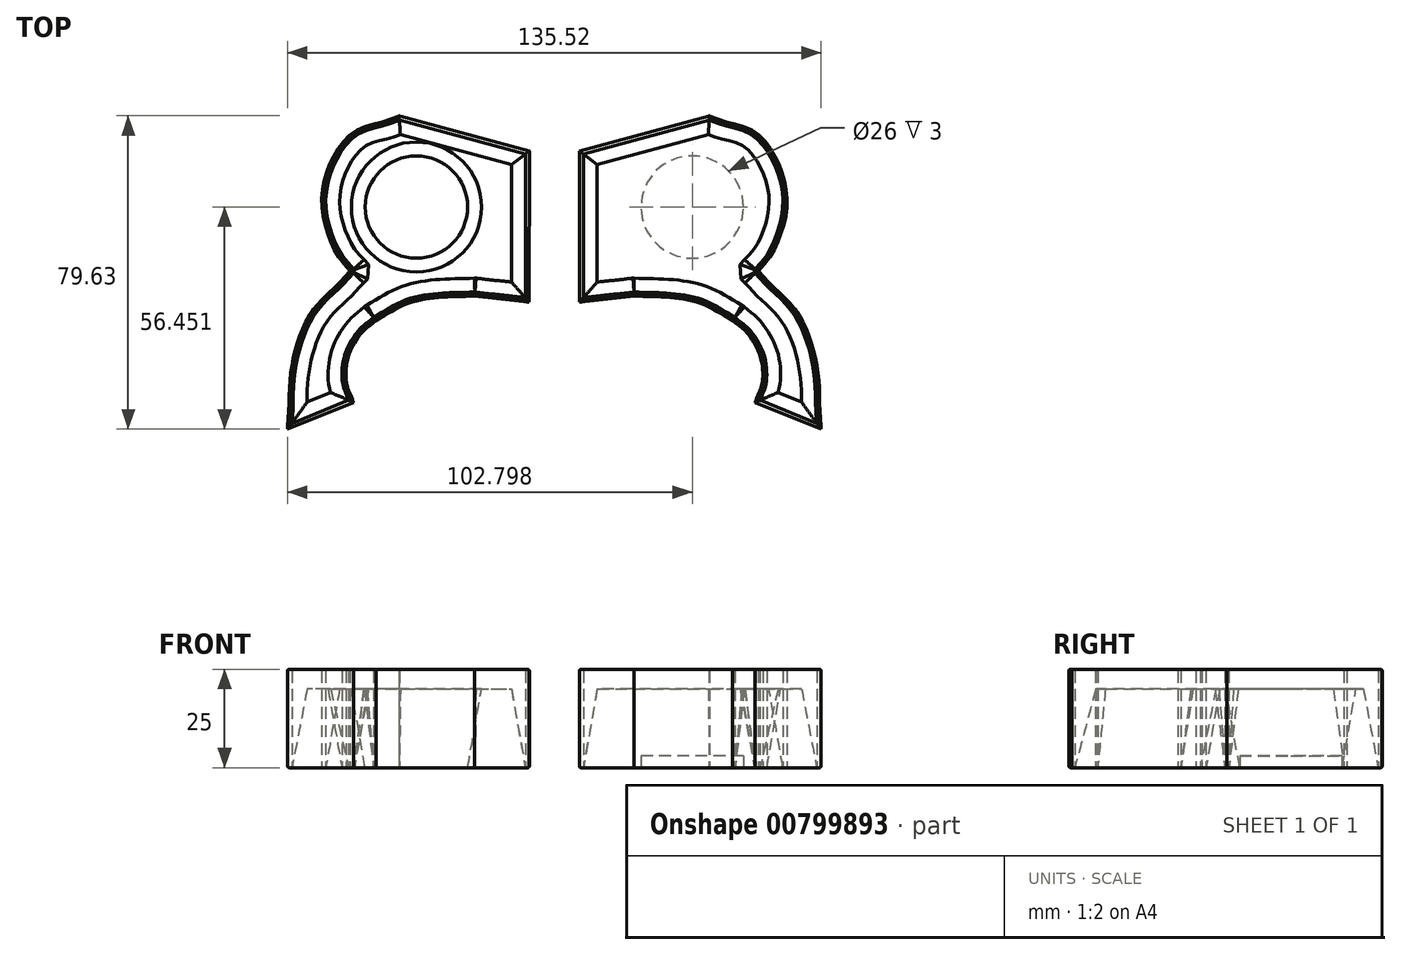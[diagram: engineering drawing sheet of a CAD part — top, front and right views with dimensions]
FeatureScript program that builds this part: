
annotation { "Feature Type Name" : "Feature", "Feature Type Description" : "" }
export const myFeature = defineFeature(function(context is Context, id is Id, definition is map)
    precondition{}
    {
        {
            var Q0;
            Q0=qCreatedBy(makeId("Top.planeOp"),FACE);
            var sketch = newSketch(context, id + "F0", { "sketchPlane" : qUnion([Q0])});
            skFitSpline(sketch, "E0", {"points": [v(6.94, -9.21) * mm, v(8.47, -9.02) * mm, v(11.5, -8.65) * mm, v(15.94, -8.2) * mm, v(18.84, -7.88) * mm, v(20.24, -7.73) * mm]});
            skFitSpline(sketch, "E1", {"points": [v(20.24, -7.73) * mm, v(23.26, -7.85) * mm, v(29.35, -8.1) * mm, v(37.98, -9.9) * mm, v(43, -12.65) * mm, v(45.29, -13.9) * mm]});
            skLineSegment(sketch, "E2", {"start": v(39.35, 38.05) * mm, "end": v(39.24, 38.02) * mm});
            skLineSegment(sketch, "E3", {"start": v(39.24, 38.02) * mm, "end": v(6.36, 29.12) * mm});
            skLineSegment(sketch, "E4", {"start": v(6.36, 29.12) * mm, "end": v(6.38, -9.28) * mm});
            skLineSegment(sketch, "E5", {"start": v(6.38, -9.28) * mm, "end": v(6.94, -9.21) * mm});
            skFitSpline(sketch, "E6", {"points": [v(45.29, -13.9) * mm, v(46.33, -14.78) * mm, v(48.35, -16.47) * mm, v(50.69, -19.57) * mm, v(52.26, -22.94) * mm, v(52.94, -26.6) * mm, v(52.67, -30.5) * mm, v(51.7, -32.98) * mm, v(51.2, -34.29) * mm]});
            skFitSpline(sketch, "E7", {"points": [v(67.73, -40.81) * mm, v(67.44, -36) * mm, v(66.88, -26.6) * mm, v(62.06, -12.45) * mm, v(55.39, -5.2) * mm, v(51.85, -1.37) * mm]});
            skLineSegment(sketch, "E8", {"start": v(51.2, -34.29) * mm, "end": v(50.99, -34.76) * mm});
            skLineSegment(sketch, "E9", {"start": v(50.99, -34.76) * mm, "end": v(67.76, -41.58) * mm});
            skLineSegment(sketch, "E10", {"start": v(67.76, -41.58) * mm, "end": v(67.73, -40.81) * mm});
            skFitSpline(sketch, "E11", {"points": [v(51.85, -1.37) * mm, v(52.8, -0.26) * mm, v(54.73, 1.97) * mm, v(56.78, 5.98) * mm, v(58.84, 12.82) * mm, v(58.12, 22.81) * mm, v(51.17, 33.76) * mm, v(43.4, 36.6) * mm, v(39.46, 38.03) * mm]});
            skLineSegment(sketch, "E12", {"start": v(39.46, 38.03) * mm, "end": v(39.35, 38.05) * mm});
            skLineSegment(sketch, "E13", {"start": v(39.35, 38.05) * mm, "end": v(39.35, 38.05) * mm});
            skLineSegment(sketch, "E14", {"start": v(39.35, 38.05) * mm, "end": v(39.46, 38.03) * mm});
            skFitSpline(sketch, "E15", {"points": [v(39.38, 37.03) * mm, v(43.13, 35.64) * mm, v(50.53, 32.9) * mm, v(57.15, 22.45) * mm, v(57.82, 12.87) * mm, v(55.83, 6.27) * mm, v(53.8, 2.36) * mm, v(51.9, 0.2) * mm, v(50.97, -0.87) * mm]});
            skLineSegment(sketch, "E16", {"start": v(50.97, -0.87) * mm, "end": v(50.81, -1.03) * mm});
            skLineSegment(sketch, "E17", {"start": v(50.81, -1.03) * mm, "end": v(50.86, -1.8) * mm});
            skLineSegment(sketch, "E18", {"start": v(50.86, -1.8) * mm, "end": v(51, -1.93) * mm});
            skLineSegment(sketch, "E19", {"start": v(51, -1.93) * mm, "end": v(50.97, -0.87) * mm});
            skFitSpline(sketch, "E20", {"points": [v(51, -1.93) * mm, v(54.47, -5.64) * mm, v(60.99, -12.63) * mm, v(65.8, -26.3) * mm, v(66.39, -35.4) * mm, v(66.69, -40.07) * mm]});
            skLineSegment(sketch, "E21", {"start": v(66.69, -40.07) * mm, "end": v(52.3, -34.22) * mm});
            skLineSegment(sketch, "E22", {"start": v(52.3, -34.22) * mm, "end": v(66.69, -40.07) * mm});
            skFitSpline(sketch, "E23", {"points": [v(52.3, -34.22) * mm, v(52.78, -32.9) * mm, v(53.7, -30.36) * mm, v(53.91, -26.39) * mm, v(53.2, -22.6) * mm, v(51.55, -19.06) * mm, v(49.1, -15.8) * mm, v(46.98, -14.02) * mm, v(45.9, -13.1) * mm]});
            skLineSegment(sketch, "E24", {"start": v(45.9, -13.1) * mm, "end": v(45.9, -13.1) * mm});
            skLineSegment(sketch, "E25", {"start": v(45.9, -13.1) * mm, "end": v(45.89, -13.1) * mm});
            skLineSegment(sketch, "E26", {"start": v(45.89, -13.1) * mm, "end": v(45.9, -13.1) * mm});
            skFitSpline(sketch, "E27", {"points": [v(45.89, -13.1) * mm, v(43.5, -11.78) * mm, v(38.35, -8.93) * mm, v(29.48, -7.07) * mm, v(23.27, -6.84) * mm, v(20.2, -6.73) * mm]});
            skLineSegment(sketch, "E28", {"start": v(20.2, -6.73) * mm, "end": v(20.18, -6.73) * mm});
            skLineSegment(sketch, "E29", {"start": v(20.18, -6.73) * mm, "end": v(20.15, -6.73) * mm});
            skLineSegment(sketch, "E30", {"start": v(20.15, -6.73) * mm, "end": v(20.2, -6.73) * mm});
            skFitSpline(sketch, "E31", {"points": [v(20.15, -6.73) * mm, v(18.82, -6.88) * mm, v(16.04, -7.2) * mm, v(11.77, -7.63) * mm, v(8.85, -7.98) * mm, v(7.38, -8.16) * mm]});
            skLineSegment(sketch, "E32", {"start": v(7.38, -8.16) * mm, "end": v(7.36, 28.36) * mm});
            skLineSegment(sketch, "E33", {"start": v(7.36, 28.36) * mm, "end": v(39.38, 37.03) * mm});
            skLineSegment(sketch, "E34", {"start": v(39.38, 37.03) * mm, "end": v(39.38, 37.03) * mm});
            skCircle(sketch, "E35", {"center": v(35.04, 14.87) * mm, "radius": 13 * mm});
            skLineSegment(sketch, "E36.MirrorCS", {"start": v(-39.35, 38.05) * mm, "end": v(-39.24, 38.02) * mm});
            skLineSegment(sketch, "E37.MirrorCS", {"start": v(-39.35, 38.05) * mm, "end": v(-39.46, 38.03) * mm});
            skLineSegment(sketch, "E38.MirrorCS", {"start": v(-45.89, -13.1) * mm, "end": v(-45.9, -13.1) * mm});
            skLineSegment(sketch, "E39.MirrorCS", {"start": v(-20.18, -6.73) * mm, "end": v(-20.15, -6.73) * mm});
            skLineSegment(sketch, "E40.MirrorCS", {"start": v(-39.46, 38.03) * mm, "end": v(-39.35, 38.05) * mm});
            skLineSegment(sketch, "E41.MirrorCS", {"start": v(-45.9, -13.1) * mm, "end": v(-45.89, -13.1) * mm});
            skLineSegment(sketch, "E42.MirrorCS", {"start": v(-20.2, -6.73) * mm, "end": v(-20.18, -6.73) * mm});
            skLineSegment(sketch, "E43.MirrorCS", {"start": v(-20.15, -6.73) * mm, "end": v(-20.2, -6.73) * mm});
            skLineSegment(sketch, "E44.MirrorCS", {"start": v(-45.9, -13.1) * mm, "end": v(-45.9, -13.1) * mm});
            skLineSegment(sketch, "E45.MirrorCS", {"start": v(-51, -1.93) * mm, "end": v(-50.97, -0.87) * mm});
            skLineSegment(sketch, "E46.MirrorCS", {"start": v(-50.81, -1.03) * mm, "end": v(-50.86, -1.8) * mm});
            skLineSegment(sketch, "E47.MirrorCS", {"start": v(-50.86, -1.8) * mm, "end": v(-51, -1.93) * mm});
            skLineSegment(sketch, "E48.MirrorCS", {"start": v(-50.97, -0.87) * mm, "end": v(-50.81, -1.03) * mm});
            skLineSegment(sketch, "E49.MirrorCS", {"start": v(-67.76, -41.58) * mm, "end": v(-67.73, -40.81) * mm});
            skLineSegment(sketch, "E50.MirrorCS", {"start": v(-51.2, -34.29) * mm, "end": v(-50.99, -34.76) * mm});
            skLineSegment(sketch, "E51.MirrorCS", {"start": v(-6.38, -9.28) * mm, "end": v(-6.94, -9.21) * mm});
            skLineSegment(sketch, "E52.MirrorCS", {"start": v(-52.3, -34.22) * mm, "end": v(-66.69, -40.07) * mm});
            skFitSpline(sketch, "E53.MirrorCS", {"points": [v(-51.85, -1.37) * mm, v(-52.8, -0.26) * mm, v(-54.73, 1.97) * mm, v(-56.78, 5.98) * mm, v(-58.84, 12.82) * mm, v(-58.12, 22.81) * mm, v(-51.17, 33.76) * mm, v(-43.4, 36.6) * mm, v(-39.46, 38.03) * mm]});
            skFitSpline(sketch, "E54.MirrorCS", {"points": [v(-39.38, 37.03) * mm, v(-43.13, 35.64) * mm, v(-50.53, 32.9) * mm, v(-57.15, 22.45) * mm, v(-57.82, 12.87) * mm, v(-55.83, 6.27) * mm, v(-53.8, 2.36) * mm, v(-51.9, 0.2) * mm, v(-50.97, -0.87) * mm]});
            skLineSegment(sketch, "E55.MirrorCS", {"start": v(-7.36, 28.36) * mm, "end": v(-39.38, 37.03) * mm});
            skCircle(sketch, "E56.MirrorC", {"center": v(-35.04, 14.87) * mm, "radius": 13 * mm});
            skLineSegment(sketch, "E57.MirrorCS", {"start": v(-50.99, -34.76) * mm, "end": v(-67.76, -41.58) * mm});
            skFitSpline(sketch, "E58.MirrorCS", {"points": [v(-51, -1.93) * mm, v(-54.47, -5.64) * mm, v(-60.99, -12.63) * mm, v(-65.8, -26.3) * mm, v(-66.39, -35.4) * mm, v(-66.69, -40.07) * mm]});
            skLineSegment(sketch, "E59.MirrorCS", {"start": v(-7.38, -8.16) * mm, "end": v(-7.36, 28.36) * mm});
            skFitSpline(sketch, "E60.MirrorCS", {"points": [v(-67.73, -40.81) * mm, v(-67.44, -36) * mm, v(-66.88, -26.6) * mm, v(-62.06, -12.45) * mm, v(-55.39, -5.2) * mm, v(-51.85, -1.37) * mm]});
            skLineSegment(sketch, "E61.MirrorCS", {"start": v(-66.69, -40.07) * mm, "end": v(-52.3, -34.22) * mm});
            skFitSpline(sketch, "E62.MirrorCS", {"points": [v(-45.29, -13.9) * mm, v(-46.33, -14.78) * mm, v(-48.35, -16.47) * mm, v(-50.69, -19.57) * mm, v(-52.26, -22.94) * mm, v(-52.94, -26.6) * mm, v(-52.67, -30.5) * mm, v(-51.7, -32.98) * mm, v(-51.2, -34.29) * mm]});
            skFitSpline(sketch, "E63.MirrorCS", {"points": [v(-20.15, -6.73) * mm, v(-18.82, -6.88) * mm, v(-16.04, -7.2) * mm, v(-11.77, -7.63) * mm, v(-8.85, -7.98) * mm, v(-7.38, -8.16) * mm]});
            skLineSegment(sketch, "E64.MirrorCS", {"start": v(-39.24, 38.02) * mm, "end": v(-6.36, 29.12) * mm});
            skLineSegment(sketch, "E65.MirrorCS", {"start": v(-6.36, 29.12) * mm, "end": v(-6.38, -9.28) * mm});
            skFitSpline(sketch, "E66.MirrorCS", {"points": [v(-52.3, -34.22) * mm, v(-52.78, -32.9) * mm, v(-53.7, -30.36) * mm, v(-53.91, -26.39) * mm, v(-53.2, -22.6) * mm, v(-51.55, -19.06) * mm, v(-49.1, -15.8) * mm, v(-46.98, -14.02) * mm, v(-45.9, -13.1) * mm]});
            skFitSpline(sketch, "E67.MirrorCS", {"points": [v(-20.24, -7.73) * mm, v(-23.26, -7.85) * mm, v(-29.35, -8.1) * mm, v(-37.98, -9.9) * mm, v(-43, -12.65) * mm, v(-45.29, -13.9) * mm]});
            skFitSpline(sketch, "E68.MirrorCS", {"points": [v(-6.94, -9.21) * mm, v(-8.47, -9.02) * mm, v(-11.5, -8.65) * mm, v(-15.94, -8.2) * mm, v(-18.84, -7.88) * mm, v(-20.24, -7.73) * mm]});
            skFitSpline(sketch, "E69.MirrorCS", {"points": [v(-45.89, -13.1) * mm, v(-43.5, -11.78) * mm, v(-38.35, -8.93) * mm, v(-29.48, -7.07) * mm, v(-23.27, -6.84) * mm, v(-20.2, -6.73) * mm]});
            skSolve(sketch);
        }
        {
            var Q0;
            Q0=makeQuery(id+"F0.imprint","IMPRINT",FACE,{"disambiguationData":[TD([[makeQuery(id+"F0.imprint","IMPRINT",EDGE,{"derivedFrom":sQuery(id+"F0.wireOp",EDGE,"E0")}),1.0]])]});
            extrude(context, id + "F1", {"entities" : qUnion([Q0]), "depth" : 25 * mm, "offsetDistance" : 25 * mm});
        }
        {
            var Q0;
            Q0=makeQuery(id+"F1.opExtrude","CAP_FACE",FACE,{"disambiguationData":[OSD([sQuery(id+"F0.wireOp",EDGE,"E0"),sQuery(id+"F0.wireOp",EDGE,"E1"),sQuery(id+"F0.wireOp",EDGE,"E2"),sQuery(id+"F0.wireOp",EDGE,"E3"),sQuery(id+"F0.wireOp",EDGE,"E4"),sQuery(id+"F0.wireOp",EDGE,"E5"),sQuery(id+"F0.wireOp",EDGE,"E6"),sQuery(id+"F0.wireOp",EDGE,"E7"),sQuery(id+"F0.wireOp",EDGE,"E8"),sQuery(id+"F0.wireOp",EDGE,"E9"),sQuery(id+"F0.wireOp",EDGE,"E10"),sQuery(id+"F0.wireOp",EDGE,"E11"),sQuery(id+"F0.wireOp",EDGE,"E14"),sQuery(id+"F0.wireOp",EDGE,"E15"),sQuery(id+"F0.wireOp",EDGE,"E19"),sQuery(id+"F0.wireOp",EDGE,"E20"),sQuery(id+"F0.wireOp",EDGE,"E22"),sQuery(id+"F0.wireOp",EDGE,"E23"),sQuery(id+"F0.wireOp",EDGE,"E26"),sQuery(id+"F0.wireOp",EDGE,"E27"),sQuery(id+"F0.wireOp",EDGE,"E30"),sQuery(id+"F0.wireOp",EDGE,"E31"),sQuery(id+"F0.wireOp",EDGE,"E32"),sQuery(id+"F0.wireOp",EDGE,"E33")])],"isStart":false});
            fillet(context, id + "F2", {"entities" : qUnion([Q0]), "radius" : .4 * mm, "tangentPropagation" : true, "allowEdgeOverflow" : false});
        }
        {
            var Q0;
            Q0=makeQuery(id+"F1.opExtrude","CAP_FACE",FACE,{"disambiguationData":[OSD([sQuery(id+"F0.wireOp",EDGE,"E0"),sQuery(id+"F0.wireOp",EDGE,"E1"),sQuery(id+"F0.wireOp",EDGE,"E2"),sQuery(id+"F0.wireOp",EDGE,"E3"),sQuery(id+"F0.wireOp",EDGE,"E4"),sQuery(id+"F0.wireOp",EDGE,"E5"),sQuery(id+"F0.wireOp",EDGE,"E6"),sQuery(id+"F0.wireOp",EDGE,"E7"),sQuery(id+"F0.wireOp",EDGE,"E8"),sQuery(id+"F0.wireOp",EDGE,"E9"),sQuery(id+"F0.wireOp",EDGE,"E10"),sQuery(id+"F0.wireOp",EDGE,"E11"),sQuery(id+"F0.wireOp",EDGE,"E14"),sQuery(id+"F0.wireOp",EDGE,"E15"),sQuery(id+"F0.wireOp",EDGE,"E19"),sQuery(id+"F0.wireOp",EDGE,"E20"),sQuery(id+"F0.wireOp",EDGE,"E22"),sQuery(id+"F0.wireOp",EDGE,"E23"),sQuery(id+"F0.wireOp",EDGE,"E26"),sQuery(id+"F0.wireOp",EDGE,"E27"),sQuery(id+"F0.wireOp",EDGE,"E30"),sQuery(id+"F0.wireOp",EDGE,"E31"),sQuery(id+"F0.wireOp",EDGE,"E32"),sQuery(id+"F0.wireOp",EDGE,"E33")])],"isStart":true});
            fillet(context, id + "F3", {"entities" : qUnion([Q0]), "radius" : .4 * mm, "tangentPropagation" : true, "allowEdgeOverflow" : false});
        }
        {
            var Q0;
            Q0=makeQuery(id+"F6WEqjFYi9otCCf_0.opExtrude","SWEPT_BODY",BODY,{"disambiguationData":[OSD([sQuery(id+"F0.wireOp",EDGE,"E15"),sQuery(id+"F0.wireOp",EDGE,"E16"),sQuery(id+"F0.wireOp",EDGE,"E17"),sQuery(id+"F0.wireOp",EDGE,"E18"),sQuery(id+"F0.wireOp",EDGE,"E20"),sQuery(id+"F0.wireOp",EDGE,"E22"),sQuery(id+"F0.wireOp",EDGE,"E23"),sQuery(id+"F0.wireOp",EDGE,"E24"),sQuery(id+"F0.wireOp",EDGE,"E25"),sQuery(id+"F0.wireOp",EDGE,"E27"),sQuery(id+"F0.wireOp",EDGE,"E28"),sQuery(id+"F0.wireOp",EDGE,"E29"),sQuery(id+"F0.wireOp",EDGE,"E31"),sQuery(id+"F0.wireOp",EDGE,"E32"),sQuery(id+"F0.wireOp",EDGE,"E33"),sQuery(id+"F0.wireOp",EDGE,"E35")])]});
            var Q1;
            Q1=makeQuery(id+"F1.opExtrude","SWEPT_BODY",BODY,{"disambiguationData":[OSD([sQuery(id+"F0.wireOp",EDGE,"E0"),sQuery(id+"F0.wireOp",EDGE,"E1"),sQuery(id+"F0.wireOp",EDGE,"E2"),sQuery(id+"F0.wireOp",EDGE,"E3"),sQuery(id+"F0.wireOp",EDGE,"E4"),sQuery(id+"F0.wireOp",EDGE,"E5"),sQuery(id+"F0.wireOp",EDGE,"E6"),sQuery(id+"F0.wireOp",EDGE,"E7"),sQuery(id+"F0.wireOp",EDGE,"E8"),sQuery(id+"F0.wireOp",EDGE,"E9"),sQuery(id+"F0.wireOp",EDGE,"E10"),sQuery(id+"F0.wireOp",EDGE,"E11"),sQuery(id+"F0.wireOp",EDGE,"E14"),sQuery(id+"F0.wireOp",EDGE,"E15"),sQuery(id+"F0.wireOp",EDGE,"E19"),sQuery(id+"F0.wireOp",EDGE,"E20"),sQuery(id+"F0.wireOp",EDGE,"E22"),sQuery(id+"F0.wireOp",EDGE,"E23"),sQuery(id+"F0.wireOp",EDGE,"E26"),sQuery(id+"F0.wireOp",EDGE,"E27"),sQuery(id+"F0.wireOp",EDGE,"E30"),sQuery(id+"F0.wireOp",EDGE,"E31"),sQuery(id+"F0.wireOp",EDGE,"E32"),sQuery(id+"F0.wireOp",EDGE,"E33")])]});
            var Q2;
            Q2=qCreatedBy(makeId("Right.planeOp"),FACE);
            mirror(context, id + "F4", {"entities" : qUnion([Q0, Q1]), "mirrorPlane" : qUnion([Q2])});
        }
        {
            var Q0;
            Q0=makeQuery(id+"F0.imprint","IMPRINT",FACE,{"disambiguationData":[TD([[makeQuery(id+"F0.imprint","IMPRINT",EDGE,{"derivedFrom":sQuery(id+"F0.wireOp",EDGE,"E15")}),-1.0]])]});
            var Q1;
            Q1=makeQuery(id+"F0.imprint","IMPRINT",FACE,{"disambiguationData":[TD([[makeQuery(id+"F0.imprint","IMPRINT",EDGE,{"derivedFrom":sQuery(id+"F0.wireOp",EDGE,"E39.MirrorCS")}),1.0]])]});
            var Q2;
            Q2=makeQuery(id+"F0.imprint","IMPRINT",FACE,{"disambiguationData":[TD([[makeQuery(id+"F0.imprint","IMPRINT",EDGE,{"derivedFrom":sQuery(id+"F0.wireOp",EDGE,"E56.MirrorC")}),-1.0]])]});
            var Q3;
            Q3=makeQuery(id+"F0.imprint","IMPRINT",FACE,{"disambiguationData":[TD([[makeQuery(id+"F0.imprint","IMPRINT",EDGE,{"derivedFrom":sQuery(id+"F0.wireOp",EDGE,"E35")}),1.0]])]});
            extrude(context, id + "F5", {"entities" : qUnion([Q0, Q1, Q2, Q3]), "depth" : 20 * mm, "offsetDistance" : 25 * mm, "hasDraft" : true, "draftAngle" : 10 * degree, "draftPullDirection" : true});
        }
        {
            var Q0;
            Q0=makeQuery(id+"F0.imprint","IMPRINT",FACE,{"disambiguationData":[TD([[makeQuery(id+"F0.imprint","IMPRINT",EDGE,{"derivedFrom":sQuery(id+"F0.wireOp",EDGE,"E35")}),1.0]])]});
            var Q1;
            Q1=makeQuery(id+"F0.imprint","IMPRINT",FACE,{"disambiguationData":[TD([[makeQuery(id+"F0.imprint","IMPRINT",EDGE,{"derivedFrom":sQuery(id+"F0.wireOp",EDGE,"E56.MirrorC")}),-1.0]])]});
            extrude(context, id + "F6", {"entities" : qUnion([Q0, Q1]), "operationType" : NewBodyOperationType.REMOVE, "depth" : 3 * mm, "offsetDistance" : 25 * mm});
        }
    });
